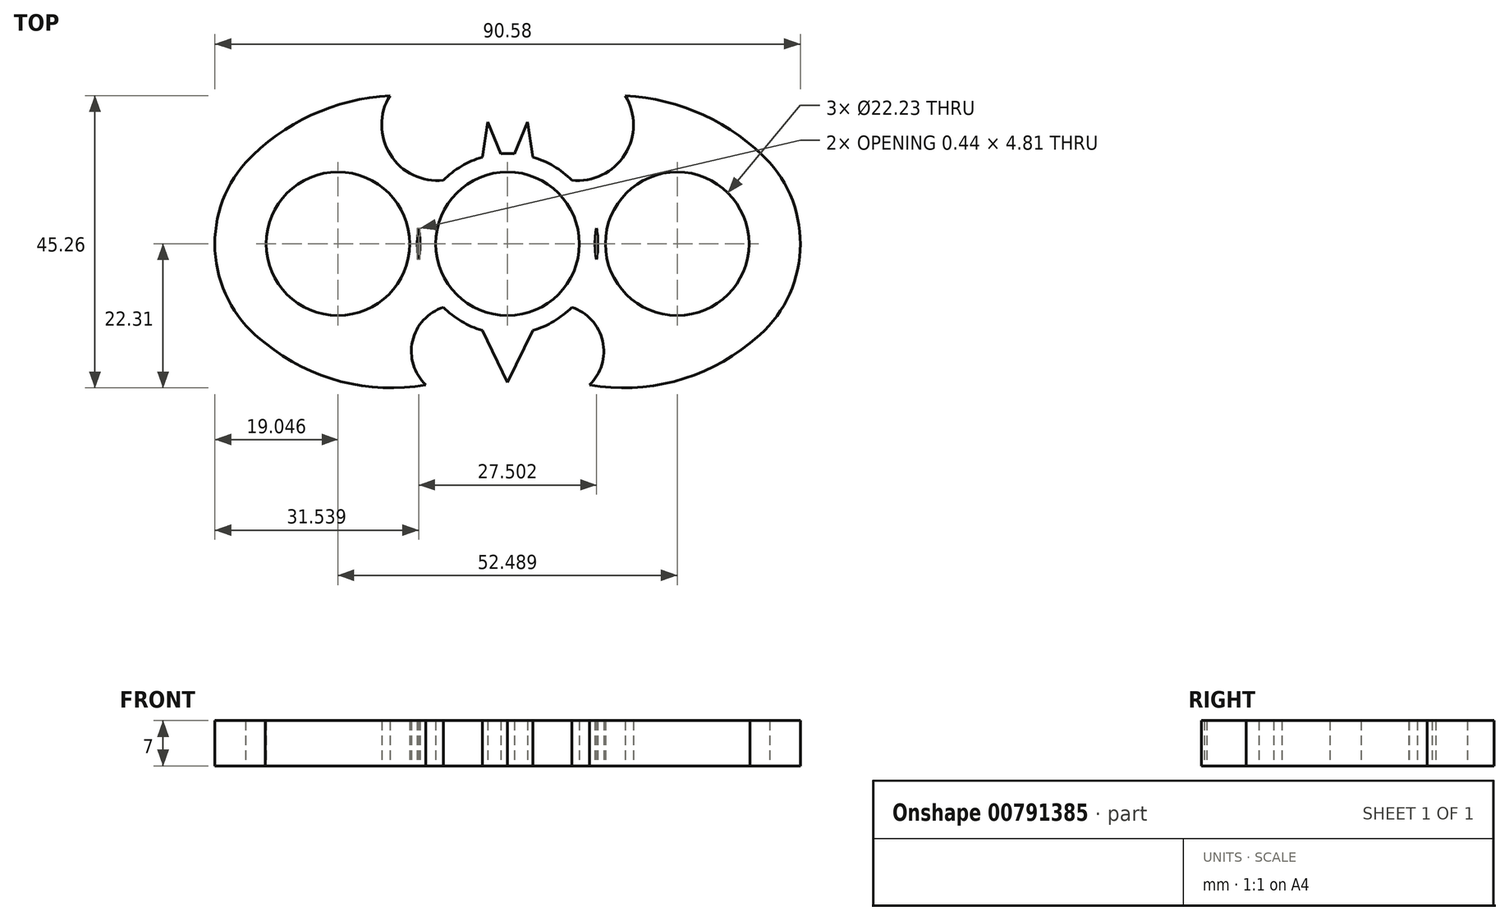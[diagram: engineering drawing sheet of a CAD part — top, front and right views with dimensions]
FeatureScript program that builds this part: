
annotation { "Feature Type Name" : "Feature", "Feature Type Description" : "" }
export const myFeature = defineFeature(function(context is Context, id is Id, definition is map)
    precondition{}
    {
        {
            var Q0;
            Q0=qCreatedBy(makeId("Top.planeOp"),FACE);
            var sketch = newSketch(context, id + "F0", { "sketchPlane" : qUnion([Q0])});
            skArc(sketch, "E0", {"start": v(-4.01, -13.38) * mm, "mid": v(7.2, 11.98) * mm, "end": v(-9.93, -9.83) * mm});
            skLineSegment(sketch, "E1", {"start": v(0, 0) * mm, "end": v(-26.24, 0) * mm});
            skLineSegment(sketch, "E2", {"start": v(0, 0) * mm, "end": v(26.24, 0) * mm});
            skArc(sketch, "E3", {"start": v(37.5, -15.37) * mm, "mid": v(45.18, -2.05) * mm, "end": v(40.53, 12.6) * mm});
            skArc(sketch, "E4", {"start": v(-18.2, 22.95) * mm, "mid": v(-30.36, 19.9) * mm, "end": v(-40.53, 12.6) * mm});
            skArc(sketch, "E5", {"start": v(-18.2, 22.95) * mm, "mid": v(-18.15, 13.81) * mm, "end": v(-9.93, 9.83) * mm});
            skArc(sketch, "E6.trimOffspring", {"start": v(-40.53, 12.6) * mm, "mid": v(-45.18, -2.05) * mm, "end": v(-37.5, -15.37) * mm});
            skArc(sketch, "E7.MirrorCS", {"start": v(18.2, 22.95) * mm, "mid": v(18.15, 13.81) * mm, "end": v(9.93, 9.83) * mm});
            skArc(sketch, "E8.MirrorCS", {"start": v(18.2, 22.95) * mm, "mid": v(30.36, 19.9) * mm, "end": v(40.53, 12.6) * mm});
            skArc(sketch, "E9", {"start": v(-37.5, -15.37) * mm, "mid": v(-25.79, -21.32) * mm, "end": v(-12.65, -21.85) * mm});
            skArc(sketch, "E10", {"start": v(-9.93, -9.83) * mm, "mid": v(-14.7, -15.06) * mm, "end": v(-12.65, -21.85) * mm});
            skArc(sketch, "E11.MirrorCS", {"start": v(9.93, -9.83) * mm, "mid": v(14.7, -15.06) * mm, "end": v(12.65, -21.85) * mm});
            skArc(sketch, "E12.MirrorCS", {"start": v(37.5, -15.37) * mm, "mid": v(25.79, -21.32) * mm, "end": v(12.65, -21.85) * mm});
            skPoint(sketch, "E13.end.orphan", {"position": v(2.34, 18.82) * mm});
            skPoint(sketch, "E14.orphan", {"position": v(3.92, 13.4) * mm});
            skPoint(sketch, "E15.end.orphan", {"position": v(-1.04, 13.93) * mm});
            skPoint(sketch, "E16.end.orphan", {"position": v(-2.23, 18.82) * mm});
            skPoint(sketch, "E17.MirrorCS.end.orphan", {"position": v(1.04, 13.93) * mm});
            skPoint(sketch, "E17.MirrorCS.start.orphan", {"position": v(2.23, 18.82) * mm});
            skPoint(sketch, "E18.end.orphan", {"position": v(-4.8, 18.35) * mm});
            skPoint(sketch, "E19.MirrorCS.end.orphan", {"position": v(4.8, 18.35) * mm});
            skLineSegment(sketch, "E20", {"start": v(-1.04, 13.93) * mm, "end": v(-3.1, 18.83) * mm});
            skLineSegment(sketch, "E21", {"start": v(-3.1, 18.83) * mm, "end": v(-3.92, 13.4) * mm});
            skLineSegment(sketch, "E22.MirrorCS", {"start": v(1.04, 13.93) * mm, "end": v(3.1, 18.83) * mm});
            skLineSegment(sketch, "E23.MirrorCS", {"start": v(3.1, 18.83) * mm, "end": v(3.92, 13.4) * mm});
            skPoint(sketch, "E24.end.orphan", {"position": v(0, -21.45) * mm});
            skPoint(sketch, "E24.start.orphan", {"position": v(-4.01, -13.38) * mm});
            skPoint(sketch, "E25.MirrorCS.start.orphan", {"position": v(4.01, -13.38) * mm});
            skPoint(sketch, "E26.MirrorCS.end.orphan", {"position": v(-3.92, -13.4) * mm});
            skPoint(sketch, "E26.MirrorCS.start.orphan", {"position": v(-3.1, -18.83) * mm});
            skLineSegment(sketch, "E27", {"start": v(-3.92, -13.4) * mm, "end": v(0, -21.45) * mm});
            skLineSegment(sketch, "E28.MirrorCS", {"start": v(3.92, -13.4) * mm, "end": v(0, -21.45) * mm});
            skLineSegment(sketch, "E29", {"start": v(0, 0) * mm, "end": v(45.3, 0) * mm});
            skArc(sketch, "E30", {"start": v(-13.76, -2.4) * mm, "mid": v(-13.53, 0) * mm, "end": v(-13.76, 2.4) * mm});
            skArc(sketch, "E31", {"start": v(13.76, 2.4) * mm, "mid": v(13.53, 0) * mm, "end": v(13.76, -2.4) * mm});
            skCircle(sketch, "E32", {"center": v(-26.24, 0) * mm, "radius": 11.11 * mm});
            skCircle(sketch, "E33", {"center": v(26.24, 0) * mm, "radius": 11.11 * mm});
            skCircle(sketch, "E34", {"center": v(0, 0) * mm, "radius": 13.97 * mm});
            skCircle(sketch, "E35", {"center": v(0, 0) * mm, "radius": 11.11 * mm});
            skSolve(sketch);
        }
        {
            var Q0;
            Q0=qSketchRegion(id+"F0",true);
            extrude(context, id + "F1", {"entities" : qUnion([Q0]), "depth" : 6.35 * mm, "offsetDistance" : 25.4 * mm});
        }
        {
            var Q0;
            Q0=makeQuery(id+"F1.opExtrude","CAP_EDGE",EDGE,{"disambiguationData":[OSD([sQuery(id+"F0.wireOp",EDGE,"E6.trimOffspring")])],"isStart":false});
            var Q1;
            Q1=makeQuery(id+"F1.opExtrude","CAP_EDGE",EDGE,{"disambiguationData":[OSD([sQuery(id+"F0.wireOp",EDGE,"E3")])],"isStart":false});
            var Q2;
            Q2=makeQuery(id+"F1.opExtrude","CAP_EDGE",EDGE,{"disambiguationData":[OSD([sQuery(id+"F0.wireOp",EDGE,"E3")])],"isStart":true});
            var Q3;
            Q3=makeQuery(id+"F1.opExtrude","CAP_EDGE",EDGE,{"disambiguationData":[OSD([sQuery(id+"F0.wireOp",EDGE,"E6.trimOffspring")])],"isStart":true});
            fillet(context, id + "F2", {"entities" : qUnion([Q0, Q1, Q2, Q3]), "radius" : 3.17 * mm, "tangentPropagation" : true, "allowEdgeOverflow" : false});
        }
        {
            var Q0;
            Q0 = qSketchRegion(id + "F0", true);
            extrude(context, id + "F3", {"entities" : qUnion([Q0]), "operationType" : NewBodyOperationType.ADD, "depth" : 7 * mm, "offsetDistance" : 25.4 * mm});
        }
    });
